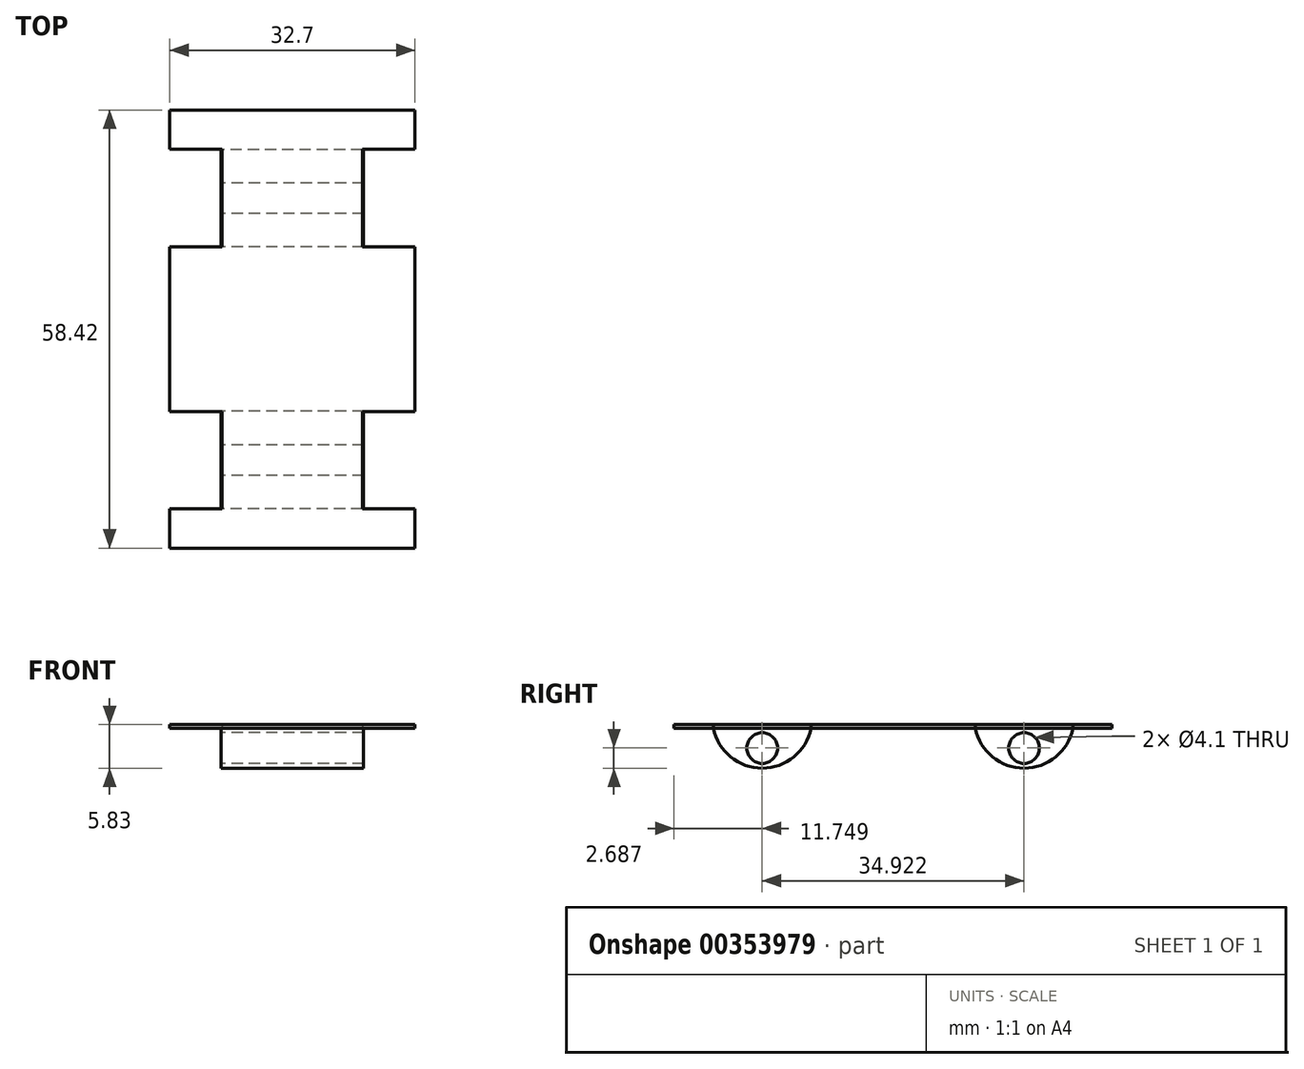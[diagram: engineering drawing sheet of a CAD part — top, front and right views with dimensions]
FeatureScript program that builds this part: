
annotation { "Feature Type Name" : "Feature", "Feature Type Description" : "" }
export const myFeature = defineFeature(function(context is Context, id is Id, definition is map)
    precondition{}
    {
        {
            var Q0;
            Q0=qCreatedBy(makeId("Top.planeOp"),FACE);
            var sketch = newSketch(context, id + "F0", { "sketchPlane" : qUnion([Q0])});
            skLineSegment(sketch, "E0.top", {"start": v(-16.35, 29.21) * mm, "end": v(16.35, 29.21) * mm});
            skLineSegment(sketch, "E0.left", {"start": v(-16.35, 0) * mm, "end": v(-16.35, 10.97) * mm});
            skLineSegment(sketch, "E0.right", {"start": v(16.35, 0) * mm, "end": v(16.35, 10.97) * mm});
            skPoint(sketch, "E0.middle", {"position": v(0, 0) * mm});
            skPoint(sketch, "E0.bottom.end.orphan", {"position": v(16.35, -29.21) * mm});
            skPoint(sketch, "E0.bottom.start.orphan", {"position": v(-16.35, -29.21) * mm});
            skLineSegment(sketch, "E1.MirrorCS", {"start": v(-16.35, -29.21) * mm, "end": v(16.35, -29.21) * mm});
            skLineSegment(sketch, "E2.MirrorCS", {"start": v(-16.35, 0) * mm, "end": v(-16.35, -10.97) * mm});
            skLineSegment(sketch, "E3.MirrorCS", {"start": v(16.35, 0) * mm, "end": v(16.35, -10.97) * mm});
            skLineSegment(sketch, "E4", {"start": v(-16.35, 23.97) * mm, "end": v(-9.35, 23.97) * mm});
            skLineSegment(sketch, "E5", {"start": v(-9.35, 23.97) * mm, "end": v(-9.35, 10.97) * mm});
            skLineSegment(sketch, "E6", {"start": v(-9.35, 10.97) * mm, "end": v(-16.35, 10.97) * mm});
            skLineSegment(sketch, "E7.MirrorCS", {"start": v(9.35, 23.97) * mm, "end": v(9.35, 10.97) * mm});
            skLineSegment(sketch, "E8.MirrorCS", {"start": v(16.35, 23.97) * mm, "end": v(9.35, 23.97) * mm});
            skLineSegment(sketch, "E9.MirrorCS", {"start": v(9.35, 10.97) * mm, "end": v(16.35, 10.97) * mm});
            skLineSegment(sketch, "E10.MirrorCS", {"start": v(-16.35, -23.97) * mm, "end": v(-9.35, -23.97) * mm});
            skLineSegment(sketch, "E11.MirrorCS", {"start": v(-9.35, -10.97) * mm, "end": v(-16.35, -10.97) * mm});
            skLineSegment(sketch, "E12.MirrorCS", {"start": v(-9.35, -23.97) * mm, "end": v(-9.35, -10.97) * mm});
            skLineSegment(sketch, "E13.MirrorCS", {"start": v(16.35, -23.97) * mm, "end": v(9.35, -23.97) * mm});
            skLineSegment(sketch, "E14.MirrorCS", {"start": v(9.35, -10.97) * mm, "end": v(16.35, -10.97) * mm});
            skLineSegment(sketch, "E15.MirrorCS", {"start": v(9.35, -23.97) * mm, "end": v(9.35, -10.97) * mm});
            skLineSegment(sketch, "E16.trimOffspring", {"start": v(-16.35, 23.97) * mm, "end": v(-16.35, 29.21) * mm});
            skLineSegment(sketch, "E17.trimOffspring", {"start": v(16.35, 23.97) * mm, "end": v(16.35, 29.21) * mm});
            skLineSegment(sketch, "E18.trimOffspring", {"start": v(16.35, -23.97) * mm, "end": v(16.35, -29.21) * mm});
            skLineSegment(sketch, "E19.trimOffspring", {"start": v(-16.35, -23.97) * mm, "end": v(-16.35, -29.21) * mm});
            skSolve(sketch);
        }
        {
            var Q0;
            Q0 = qSketchRegion(id + "F0", true);
            extrude(context, id + "F1", {"entities" : qUnion([Q0]), "depth" : .5 * mm});
        }
        {
            var Q0;
            Q0=qCreatedBy(makeId("Right.planeOp"),FACE);
            var sketch = newSketch(context, id + "F2", { "sketchPlane" : qUnion([Q0])});
            skArc(sketch, "E20", {"start": v(10.96, 0) * mm, "mid": v(17.46, -5.33) * mm, "end": v(23.96, 0) * mm});
            skLineSegment(sketch, "E21", {"start": v(23.96, 0) * mm, "end": v(10.96, 0) * mm});
            skPoint(sketch, "E22.centerSnap0", {"position": v(17.46, 0) * mm});
            skPoint(sketch, "E23.MirrorCS.end.orphan", {"position": v(24, 0.5) * mm});
            skPoint(sketch, "E23.MirrorCS.start.orphan", {"position": v(10.9, 0.45) * mm});
            skPoint(sketch, "E24.end.orphan", {"position": v(-24, 0.5) * mm});
            skPoint(sketch, "E24.start.orphan", {"position": v(-10.9, 0.45) * mm});
            skArc(sketch, "E25.MirrorCS", {"start": v(-10.96, 0) * mm, "mid": v(-17.46, -5.33) * mm, "end": v(-23.96, 0) * mm});
            skPoint(sketch, "E22.center.orphan", {"position": v(17.46, -2.64) * mm});
            skCircle(sketch, "E26", {"center": v(17.46, -2.64) * mm, "radius": 2.05 * mm});
            skCircle(sketch, "E27.MirrorC", {"center": v(-17.46, -2.64) * mm, "radius": 2.05 * mm});
            skLineSegment(sketch, "E28.MirrorCS", {"start": v(-23.96, 0) * mm, "end": v(-10.96, 0) * mm});
            skSolve(sketch);
        }
        {
            var Q0;
            Q0 = qSketchRegion(id + "F2", true);
            extrude(context, id + "F3", {"entities" : qUnion([Q0]), "operationType" : NewBodyOperationType.ADD, "endBound" : BoundingType.SYMMETRIC, "depth" : 19 * mm});
        }
    });
